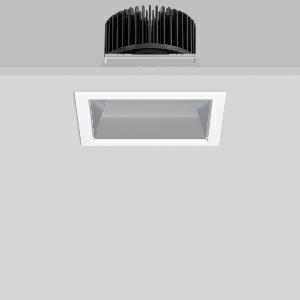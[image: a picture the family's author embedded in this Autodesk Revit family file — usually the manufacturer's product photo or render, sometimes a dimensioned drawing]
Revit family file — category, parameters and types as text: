
# Revit family: quardo_901706_002_1_b3a9
name_source: partatom
category: Lighting Fixtures
units: mm (PartAtom-declared; Revit-internal decimal feet)

## family parameters
Cut with Voids When Loaded = No
Host = Face
Light Source = No
Part Type = Normal
Room Calculation Point = No
Round Connector Dimension = Use Diameter
Shared = No

## types (1)
- QUARDO (1 x LED Modul 840, 4450 lm, 4000)
    Apparent Load = 37 VA
    CIE Flux Codes = 81 100 100 100 100
    Color Rendering = 80
    Color Temperature = 4000
    Default Elevation = 1800 mm
    Description = Series: QUARDO
High-quality recessed downlight with square luminous surface. Recessed mounting frame: die-cast aluminium, powder-coated. Mounting bracket: galvanised sheet steel. Reflector: aluminium, highly polished anodised finish. Ceiling installation with spring system. Including separate LED converter with connecting cable 600 mm. Through-wiring box (5 pole) available as accessory. 
Colour: traffic white, matt (RAL 9016)
Length: 176 mm
Width: 176 mm
Height: 4 mm
Cut-out length: 165 mm
Cut-out width: 165 mm
Recess height: 150 mm
Luminaire: recess height: 145 mm
Lamp: LED
Socket: without socket
Colour temperature: 4000K
Colour rendering index (CRI): 85
System power: 37 W
Rated luminous flux: 4450 lm
Luminous efficiency: 120 lm/W
Control gear: Regulated power supply
Protection class: II
Type of protection: IP 20
    Height = 0 mm  [stored 0 ft]
    Lamp = 1 x LED Modul 840
    Lamp Light Flux = 4450 lm
    Lamp count = 1
    Length = 176 mm
    Lifetime = 50000 h
    Luminous efficacy = 120 lm/W
    Manufacturer = RZB
    ModVariant = No
    Model = 901706.002.1
    Mounting Place = Ceiling
    Mounting Type = Recessed
    Number of Poles = 1
    OnlyDefault = Yes
    Power Factor = 1
    Product Name = QUARDO
    Product group = Recessed downlights
    ProductGroupID = 402
    Protection Class = Protection class II
    Protection Degree = IP 20
    RLX_Detail_Level = 1
    RLX_Emergency_Light_Flux = 0 lm
    RLX_Emergency_Type = 0
    RLX_Emergency_Type_DB = No
    RlxData = <blob elided: 29285 chars, md5=0ecceb82>
    Socket = socket
    Standby Power = 0 W
    System Light Flux = 4450 lm
    System Power = 37 W
    Type Comments = Product without accessories
    Type Image = 901705.002.jpg
    URL = http://relux.com
    VarID = ---
    Voltage = 230 V
    Voltage Range = 220-240 V
    Weight = 0.00 kg
    Width = 176 mm

note: [stored X ft] marks values corroborated as IEEE doubles in the binary element streams (Revit-internal decimal feet)

## geometry (parser evidence)
native form markers: Blend x4, Sweep x9
no freeform markers — native parametric forms only
